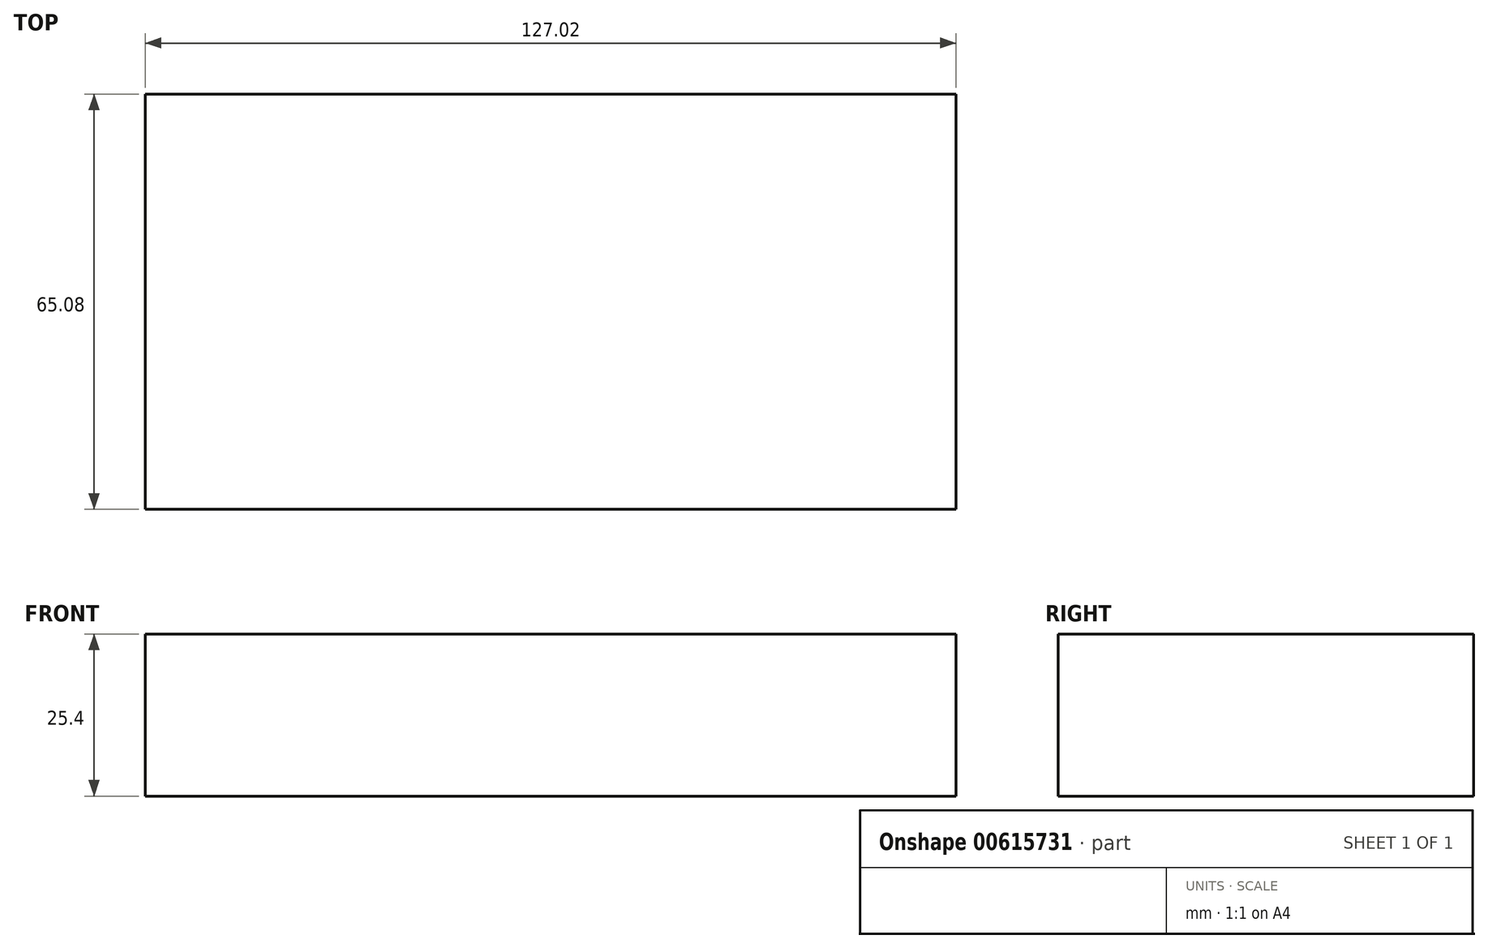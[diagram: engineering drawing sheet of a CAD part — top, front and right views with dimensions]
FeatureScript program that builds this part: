
annotation { "Feature Type Name" : "Feature", "Feature Type Description" : "" }
export const myFeature = defineFeature(function(context is Context, id is Id, definition is map)
    precondition{}
    {
        {
            var Q0;
            Q0=qCreatedBy(makeId("Top.planeOp"),FACE);
            var sketch = newSketch(context, id + "F0", { "sketchPlane" : qUnion([Q0])});
            skLineSegment(sketch, "E0.bottom", {"start": v(63.51, 32.54) * mm, "end": v(-63.51, 32.54) * mm});
            skLineSegment(sketch, "E0.top", {"start": v(63.51, -32.54) * mm, "end": v(-63.51, -32.54) * mm});
            skLineSegment(sketch, "E0.left", {"start": v(63.51, 32.54) * mm, "end": v(63.51, -32.54) * mm});
            skLineSegment(sketch, "E0.right", {"start": v(-63.51, 32.54) * mm, "end": v(-63.51, -32.54) * mm});
            skPoint(sketch, "E0.middle", {"position": v(0, 0) * mm});
            skSolve(sketch);
        }
        {
            var Q0;
            Q0=makeQuery(id+"F0.imprint","IMPRINT",FACE,{"disambiguationData":[TD([[makeQuery(id+"F0.imprint","IMPRINT",EDGE,{"derivedFrom":sQuery(id+"F0.wireOp",EDGE,"E0.bottom")}),1.0]])]});
            extrude(context, id + "F1", {"entities" : qUnion([Q0]), "depth" : 25.4 * mm, "offsetDistance" : 25.4 * mm});
        }
    });
